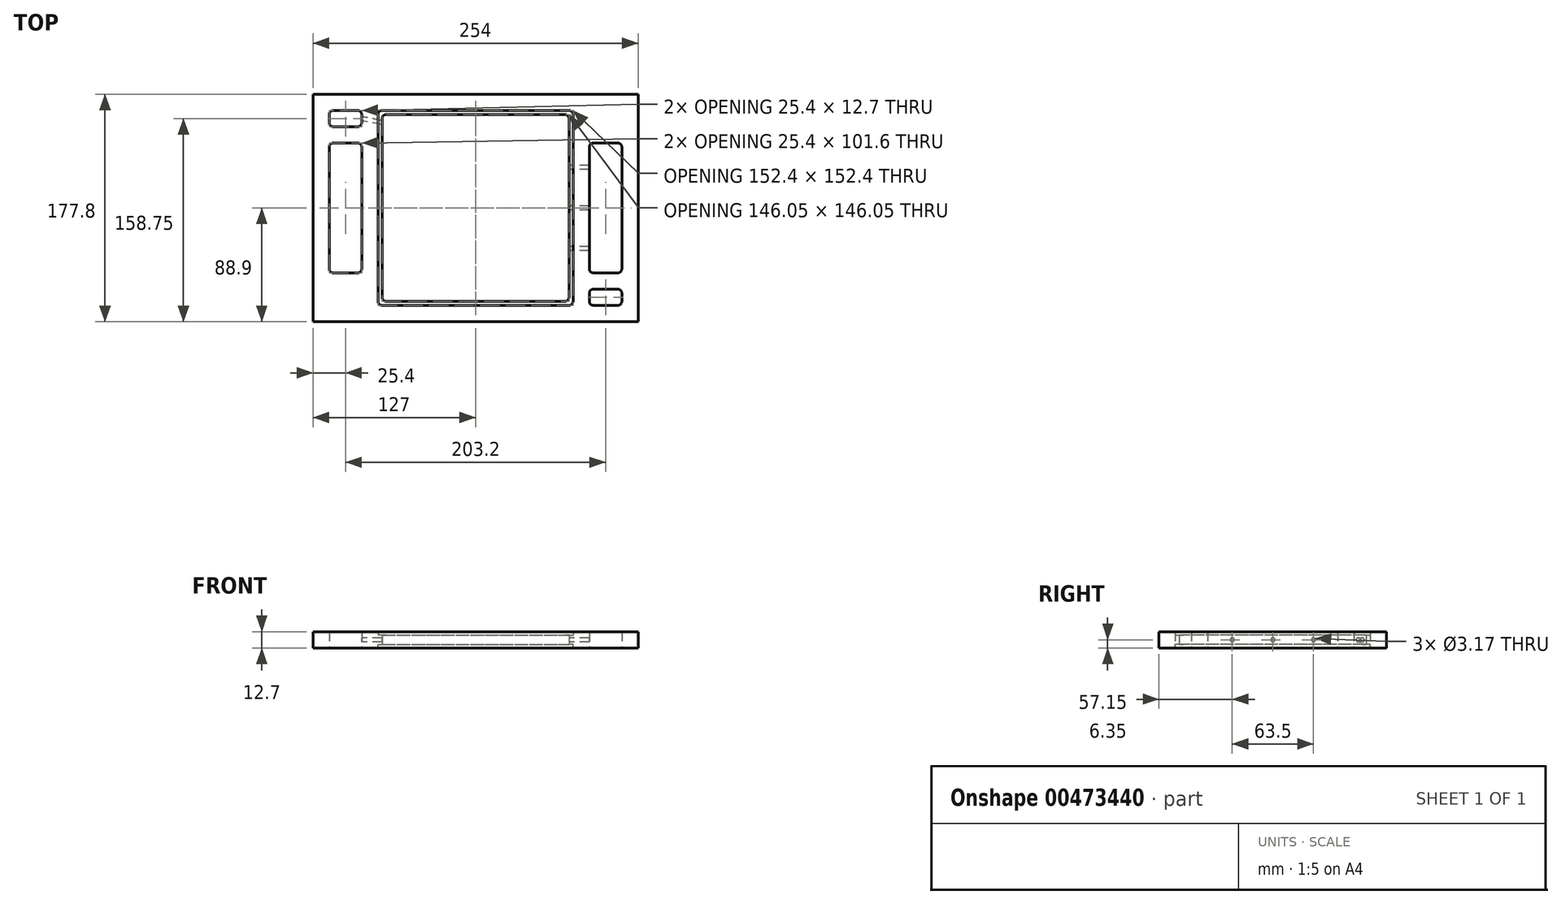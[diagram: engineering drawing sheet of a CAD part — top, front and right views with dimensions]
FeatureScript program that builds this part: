
annotation { "Feature Type Name" : "Feature", "Feature Type Description" : "" }
export const myFeature = defineFeature(function(context is Context, id is Id, definition is map)
    precondition{}
    {
        {
            var Q0;
            Q0=qCreatedBy(makeId("Top.planeOp"),FACE);
            var sketch = newSketch(context, id + "F0", { "sketchPlane" : qUnion([Q0])});
            skPoint(sketch, "E0.middle", {"position": v(0, 0) * mm});
            skLineSegment(sketch, "E1.bottom", {"start": v(-76.2, 76.2) * mm, "end": v(76.2, 76.2) * mm});
            skLineSegment(sketch, "E1.top", {"start": v(-76.2, -76.2) * mm, "end": v(76.2, -76.2) * mm});
            skLineSegment(sketch, "E1.left", {"start": v(-76.2, 76.2) * mm, "end": v(-76.2, -76.2) * mm});
            skLineSegment(sketch, "E1.right", {"start": v(76.2, 76.2) * mm, "end": v(76.2, -76.2) * mm});
            skLineSegment(sketch, "E2.bottom", {"start": v(-127, 88.9) * mm, "end": v(127, 88.9) * mm});
            skLineSegment(sketch, "E2.top", {"start": v(-127, -88.9) * mm, "end": v(127, -88.9) * mm});
            skLineSegment(sketch, "E2.left", {"start": v(-127, 88.9) * mm, "end": v(-127, -88.9) * mm});
            skLineSegment(sketch, "E2.right", {"start": v(127, 88.9) * mm, "end": v(127, -88.9) * mm});
            skLineSegment(sketch, "E3.bottom", {"start": v(-88.9, 76.2) * mm, "end": v(-114.3, 76.2) * mm});
            skLineSegment(sketch, "E3.top", {"start": v(-88.9, 63.5) * mm, "end": v(-114.3, 63.5) * mm});
            skLineSegment(sketch, "E3.left", {"start": v(-88.9, 76.2) * mm, "end": v(-88.9, 63.5) * mm});
            skLineSegment(sketch, "E3.right", {"start": v(-114.3, 76.2) * mm, "end": v(-114.3, 63.5) * mm});
            skLineSegment(sketch, "E4", {"start": v(0, 76.2) * mm, "end": v(0, -76.2) * mm, "construction": true});
            skLineSegment(sketch, "E5", {"start": v(-76.2, 0) * mm, "end": v(76.2, 0) * mm, "construction": true});
            skLineSegment(sketch, "E6.bottom", {"start": v(88.9, -76.2) * mm, "end": v(114.3, -76.2) * mm});
            skLineSegment(sketch, "E6.top", {"start": v(88.9, -63.5) * mm, "end": v(114.3, -63.5) * mm});
            skLineSegment(sketch, "E6.left", {"start": v(88.9, -76.2) * mm, "end": v(88.9, -63.5) * mm});
            skLineSegment(sketch, "E6.right", {"start": v(114.3, -76.2) * mm, "end": v(114.3, -63.5) * mm});
            skLineSegment(sketch, "E7.bottom", {"start": v(-88.9, 50.8) * mm, "end": v(-114.3, 50.8) * mm});
            skLineSegment(sketch, "E7.top", {"start": v(-88.9, -50.8) * mm, "end": v(-114.3, -50.8) * mm});
            skLineSegment(sketch, "E7.left", {"start": v(-88.9, 50.8) * mm, "end": v(-88.9, -50.8) * mm});
            skLineSegment(sketch, "E7.right", {"start": v(-114.3, 50.8) * mm, "end": v(-114.3, -50.8) * mm});
            skPoint(sketch, "E7.middle", {"position": v(-101.6, 0) * mm});
            skLineSegment(sketch, "E8.MirrorCS", {"start": v(88.9, 50.8) * mm, "end": v(114.3, 50.8) * mm});
            skLineSegment(sketch, "E9.MirrorCS", {"start": v(114.3, 50.8) * mm, "end": v(114.3, -50.8) * mm});
            skLineSegment(sketch, "E10.MirrorCS", {"start": v(88.9, 50.8) * mm, "end": v(88.9, -50.8) * mm});
            skLineSegment(sketch, "E11.MirrorCS", {"start": v(88.9, -50.8) * mm, "end": v(114.3, -50.8) * mm});
            skSolve(sketch);
        }
        {
            var Q0;
            Q0=makeQuery(id+"F0.imprint","IMPRINT",FACE,{"disambiguationData":[TD([[makeQuery(id+"F0.imprint","IMPRINT",EDGE,{"derivedFrom":sQuery(id+"F0.wireOp",EDGE,"E1.bottom")}),1.0]])]});
            extrude(context, id + "F1", {"entities" : qUnion([Q0]), "depth" : 6.35 * mm, "offsetDistance" : 25.4 * mm});
        }
        {
            var Q0;
            Q0=makeQuery(id+"F0.imprint","IMPRINT",FACE,{"disambiguationData":[TD([[makeQuery(id+"F0.imprint","IMPRINT",EDGE,{"derivedFrom":sQuery(id+"F0.wireOp",EDGE,"E1.bottom")}),-1.0]])]});
            var sketch = newSketch(context, id + "F2", { "sketchPlane" : qUnion([Q0])});
            skLineSegment(sketch, "E12.0", {"start": v(-76.2, 76.2) * mm, "end": v(76.2, 76.2) * mm});
            skLineSegment(sketch, "E12.1", {"start": v(-76.2, 76.2) * mm, "end": v(-76.2, -76.2) * mm});
            skLineSegment(sketch, "E12.2", {"start": v(76.2, 76.2) * mm, "end": v(76.2, -76.2) * mm});
            skLineSegment(sketch, "E12.3", {"start": v(-76.2, -76.2) * mm, "end": v(76.2, -76.2) * mm});
            skLineSegment(sketch, "E13.0", {"start": v(-73.03, 73.02) * mm, "end": v(73.03, 73.03) * mm});
            skLineSegment(sketch, "E13.1", {"start": v(-73.03, 73.02) * mm, "end": v(-73.03, -73.03) * mm});
            skLineSegment(sketch, "E13.2", {"start": v(-73.03, -73.03) * mm, "end": v(73.03, -73.02) * mm});
            skLineSegment(sketch, "E13.3", {"start": v(73.03, 73.03) * mm, "end": v(73.03, -73.02) * mm});
            skSolve(sketch);
        }
        {
            var Q0;
            Q0=makeQuery(id+"F2.imprint","IMPRINT",FACE,{"disambiguationData":[TD([[makeQuery(id+"F2.imprint","IMPRINT",EDGE,{"derivedFrom":sQuery(id+"F2.wireOp",EDGE,"E12.0")}),-1.0]])]});
            extrude(context, id + "F3", {"entities" : qUnion([Q0]), "operationType" : NewBodyOperationType.ADD, "depth" : 3.56 * mm, "offsetDistance" : 25.4 * mm});
        }
        {
            var Q0;
            {var subQ0=makeQuery(id+"F3.opExtrude","SWEPT_EDGE",EDGE,{"disambiguationData":[OSD([sQuery(id+"F2.wireOp",EDGE,"E13.0"),sQuery(id+"F2.wireOp",EDGE,"E13.1")])]});Q0=makeQuery(id+"F6.boolean.opBoolean","MERGE",EDGE,{"derivedFrom":[subQ0,makeQuery(id+"F6.opPattern","COPY",EDGE,{"derivedFrom":subQ0,"instanceName":"1"})]});}
            var Q1;
            Q1=makeQuery(id+"F1.opExtrude","SWEPT_EDGE",EDGE,{"disambiguationData":[OSD([sQuery(id+"F0.wireOp",EDGE,"E1.bottom"),sQuery(id+"F0.wireOp",EDGE,"E1.left")])]});
            var Q2;
            Q2=makeQuery(id+"F3.opExtrude","SWEPT_EDGE",EDGE,{"disambiguationData":[OSD([sQuery(id+"F2.wireOp",EDGE,"E13.0"),sQuery(id+"F2.wireOp",EDGE,"E13.3")])]});
            var Q3;
            Q3=makeQuery(id+"F1.opExtrude","SWEPT_EDGE",EDGE,{"disambiguationData":[OSD([sQuery(id+"F0.wireOp",EDGE,"E1.bottom"),sQuery(id+"F0.wireOp",EDGE,"E1.right")])]});
            var Q4;
            Q4=makeQuery(id+"F3.opExtrude","SWEPT_EDGE",EDGE,{"disambiguationData":[OSD([sQuery(id+"F2.wireOp",EDGE,"E13.1"),sQuery(id+"F2.wireOp",EDGE,"E13.2")])]});
            var Q5;
            Q5=makeQuery(id+"F1.opExtrude","SWEPT_EDGE",EDGE,{"disambiguationData":[OSD([sQuery(id+"F0.wireOp",EDGE,"E1.top"),sQuery(id+"F0.wireOp",EDGE,"E1.left")])]});
            var Q6;
            Q6=makeQuery(id+"F3.opExtrude","SWEPT_EDGE",EDGE,{"disambiguationData":[OSD([sQuery(id+"F2.wireOp",EDGE,"E13.2"),sQuery(id+"F2.wireOp",EDGE,"E13.3")])]});
            var Q7;
            Q7=makeQuery(id+"F1.opExtrude","SWEPT_EDGE",EDGE,{"disambiguationData":[OSD([sQuery(id+"F0.wireOp",EDGE,"E1.top"),sQuery(id+"F0.wireOp",EDGE,"E1.right")])]});
            fillet(context, id + "F4", {"entities" : qUnion([Q0, Q1, Q2, Q3, Q4, Q5, Q6, Q7]), "radius" : 3.17 * mm, "tangentPropagation" : true, "allowEdgeOverflow" : false});
        }
        {
            var Q0;
            Q0=makeQuery(id+"F1.opExtrude","SWEPT_EDGE",EDGE,{"disambiguationData":[OSD([sQuery(id+"F0.wireOp",EDGE,"E3.bottom"),sQuery(id+"F0.wireOp",EDGE,"E3.left")])]});
            var Q1;
            Q1=makeQuery(id+"F1.opExtrude","SWEPT_EDGE",EDGE,{"disambiguationData":[OSD([sQuery(id+"F0.wireOp",EDGE,"E3.top"),sQuery(id+"F0.wireOp",EDGE,"E3.left")])]});
            var Q2;
            Q2=makeQuery(id+"F1.opExtrude","SWEPT_EDGE",EDGE,{"disambiguationData":[OSD([sQuery(id+"F0.wireOp",EDGE,"E3.top"),sQuery(id+"F0.wireOp",EDGE,"E3.right")])]});
            var Q3;
            Q3=makeQuery(id+"F1.opExtrude","SWEPT_EDGE",EDGE,{"disambiguationData":[OSD([sQuery(id+"F0.wireOp",EDGE,"E3.bottom"),sQuery(id+"F0.wireOp",EDGE,"E3.right")])]});
            var Q4;
            Q4=makeQuery(id+"F1.opExtrude","SWEPT_EDGE",EDGE,{"disambiguationData":[OSD([sQuery(id+"F0.wireOp",EDGE,"E7.bottom"),sQuery(id+"F0.wireOp",EDGE,"E7.right")])]});
            var Q5;
            Q5=makeQuery(id+"F1.opExtrude","SWEPT_EDGE",EDGE,{"disambiguationData":[OSD([sQuery(id+"F0.wireOp",EDGE,"E7.bottom"),sQuery(id+"F0.wireOp",EDGE,"E7.left")])]});
            var Q6;
            Q6=makeQuery(id+"F1.opExtrude","SWEPT_EDGE",EDGE,{"disambiguationData":[OSD([sQuery(id+"F0.wireOp",EDGE,"E7.top"),sQuery(id+"F0.wireOp",EDGE,"E7.left")])]});
            var Q7;
            Q7=makeQuery(id+"F1.opExtrude","SWEPT_EDGE",EDGE,{"disambiguationData":[OSD([sQuery(id+"F0.wireOp",EDGE,"E7.top"),sQuery(id+"F0.wireOp",EDGE,"E7.right")])]});
            var Q8;
            Q8=makeQuery(id+"F1.opExtrude","SWEPT_EDGE",EDGE,{"disambiguationData":[OSD([sQuery(id+"F0.wireOp",EDGE,"E6.bottom"),sQuery(id+"F0.wireOp",EDGE,"E6.right")])]});
            var Q9;
            Q9=makeQuery(id+"F1.opExtrude","SWEPT_EDGE",EDGE,{"disambiguationData":[OSD([sQuery(id+"F0.wireOp",EDGE,"E6.bottom"),sQuery(id+"F0.wireOp",EDGE,"E6.left")])]});
            var Q10;
            Q10=makeQuery(id+"F1.opExtrude","SWEPT_EDGE",EDGE,{"disambiguationData":[OSD([sQuery(id+"F0.wireOp",EDGE,"E6.top"),sQuery(id+"F0.wireOp",EDGE,"E6.left")])]});
            var Q11;
            Q11=makeQuery(id+"F1.opExtrude","SWEPT_EDGE",EDGE,{"disambiguationData":[OSD([sQuery(id+"F0.wireOp",EDGE,"E6.top"),sQuery(id+"F0.wireOp",EDGE,"E6.right")])]});
            var Q12;
            Q12=makeQuery(id+"F1.opExtrude","SWEPT_EDGE",EDGE,{"disambiguationData":[OSD([sQuery(id+"F0.wireOp",EDGE,"E9.MirrorCS"),sQuery(id+"F0.wireOp",EDGE,"E11.MirrorCS")])]});
            var Q13;
            Q13=makeQuery(id+"F1.opExtrude","SWEPT_EDGE",EDGE,{"disambiguationData":[OSD([sQuery(id+"F0.wireOp",EDGE,"E10.MirrorCS"),sQuery(id+"F0.wireOp",EDGE,"E11.MirrorCS")])]});
            var Q14;
            Q14=makeQuery(id+"F1.opExtrude","SWEPT_EDGE",EDGE,{"disambiguationData":[OSD([sQuery(id+"F0.wireOp",EDGE,"E8.MirrorCS"),sQuery(id+"F0.wireOp",EDGE,"E10.MirrorCS")])]});
            var Q15;
            Q15=makeQuery(id+"F1.opExtrude","SWEPT_EDGE",EDGE,{"disambiguationData":[OSD([sQuery(id+"F0.wireOp",EDGE,"E8.MirrorCS"),sQuery(id+"F0.wireOp",EDGE,"E9.MirrorCS")])]});
            fillet(context, id + "F5", {"entities" : qUnion([Q0, Q1, Q2, Q3, Q4, Q5, Q6, Q7, Q8, Q9, Q10, Q11, Q12, Q13, Q14, Q15]), "radius" : 3.17 * mm, "allowEdgeOverflow" : false});
        }
        {
            var Q0;
            Q0=makeQuery(id+"F1.opExtrude","SWEPT_BODY",BODY,{"disambiguationData":[OSD([sQuery(id+"F0.wireOp",EDGE,"E1.bottom"),sQuery(id+"F0.wireOp",EDGE,"E1.top"),sQuery(id+"F0.wireOp",EDGE,"E1.left"),sQuery(id+"F0.wireOp",EDGE,"E1.right"),sQuery(id+"F0.wireOp",EDGE,"E2.bottom"),sQuery(id+"F0.wireOp",EDGE,"E2.top"),sQuery(id+"F0.wireOp",EDGE,"E2.left"),sQuery(id+"F0.wireOp",EDGE,"E2.right"),sQuery(id+"F0.wireOp",EDGE,"E3.bottom"),sQuery(id+"F0.wireOp",EDGE,"E3.top"),sQuery(id+"F0.wireOp",EDGE,"E3.left"),sQuery(id+"F0.wireOp",EDGE,"E3.right"),sQuery(id+"F0.wireOp",EDGE,"E6.bottom"),sQuery(id+"F0.wireOp",EDGE,"E6.top"),sQuery(id+"F0.wireOp",EDGE,"E6.left"),sQuery(id+"F0.wireOp",EDGE,"E6.right"),sQuery(id+"F0.wireOp",EDGE,"E7.bottom"),sQuery(id+"F0.wireOp",EDGE,"E7.top"),sQuery(id+"F0.wireOp",EDGE,"E7.left"),sQuery(id+"F0.wireOp",EDGE,"E7.right"),sQuery(id+"F0.wireOp",EDGE,"E8.MirrorCS"),sQuery(id+"F0.wireOp",EDGE,"E9.MirrorCS"),sQuery(id+"F0.wireOp",EDGE,"E10.MirrorCS"),sQuery(id+"F0.wireOp",EDGE,"E11.MirrorCS")])]});
            var Q1;
            Q1=makeQuery(id+"F0.imprint","IMPRINT",FACE,{"disambiguationData":[TD([[makeQuery(id+"F0.imprint","IMPRINT",EDGE,{"derivedFrom":sQuery(id+"F0.wireOp",EDGE,"E1.bottom")}),-1.0]])]});
            mirror(context, id + "F6", {"operationType" : NewBodyOperationType.ADD, "entities" : qUnion([Q0]), "mirrorPlane" : qUnion([Q1])});
        }
        {
            var Q0;
            {var subQ0=makeQuery(id+"F3.opExtrude","SWEPT_FACE",FACE,{"disambiguationData":[OSD([sQuery(id+"F2.wireOp",EDGE,"E13.3")])]});Q0=makeQuery(id+"F6.boolean.opBoolean","MERGE",FACE,{"derivedFrom":[subQ0,makeQuery(id+"F6.opPattern","COPY",FACE,{"derivedFrom":subQ0,"instanceName":"1"})]});}
            var sketch = newSketch(context, id + "F7", { "sketchPlane" : qUnion([Q0])});
            skLineSegment(sketch, "E14.0", {"start": v(-69.85, 0) * mm, "end": v(69.85, 0) * mm});
            skPoint(sketch, "E15", {"position": v(0, 0) * mm});
            skPoint(sketch, "E16", {"position": v(-31.75, 0) * mm});
            skPoint(sketch, "E17.MirrorP", {"position": v(31.75, 0) * mm});
            skSolve(sketch);
        }
        {
            var Q0;
            Q0=sQuery(id+"F7.wireOp",VERTEX,"E16");
            var Q1;
            Q1=sQuery(id+"F7.wireOp",VERTEX,"E15");
            var Q2;
            Q2=sQuery(id+"F7.wireOp",VERTEX,"E17.MirrorP");
            var Q3;
            Q3=makeQuery(id+"F1.opExtrude","SWEPT_BODY",BODY,{"disambiguationData":[OSD([sQuery(id+"F0.wireOp",EDGE,"E1.bottom"),sQuery(id+"F0.wireOp",EDGE,"E1.top"),sQuery(id+"F0.wireOp",EDGE,"E1.left"),sQuery(id+"F0.wireOp",EDGE,"E1.right"),sQuery(id+"F0.wireOp",EDGE,"E2.bottom"),sQuery(id+"F0.wireOp",EDGE,"E2.top"),sQuery(id+"F0.wireOp",EDGE,"E2.left"),sQuery(id+"F0.wireOp",EDGE,"E2.right"),sQuery(id+"F0.wireOp",EDGE,"E3.bottom"),sQuery(id+"F0.wireOp",EDGE,"E3.top"),sQuery(id+"F0.wireOp",EDGE,"E3.left"),sQuery(id+"F0.wireOp",EDGE,"E3.right"),sQuery(id+"F0.wireOp",EDGE,"E6.bottom"),sQuery(id+"F0.wireOp",EDGE,"E6.top"),sQuery(id+"F0.wireOp",EDGE,"E6.left"),sQuery(id+"F0.wireOp",EDGE,"E6.right"),sQuery(id+"F0.wireOp",EDGE,"E7.bottom"),sQuery(id+"F0.wireOp",EDGE,"E7.top"),sQuery(id+"F0.wireOp",EDGE,"E7.left"),sQuery(id+"F0.wireOp",EDGE,"E7.right"),sQuery(id+"F0.wireOp",EDGE,"E8.MirrorCS"),sQuery(id+"F0.wireOp",EDGE,"E9.MirrorCS"),sQuery(id+"F0.wireOp",EDGE,"E10.MirrorCS"),sQuery(id+"F0.wireOp",EDGE,"E11.MirrorCS")])]});
            hole(context, id + "F8", {"style" : HoleStyle.SIMPLE, "endStyle" : HoleEndStyle.BLIND, "holeDiameter" : 3.17 * mm, "majorDiameter" : 6.35 * mm, "holeDepth" : 19.05 * mm, "isTappedThrough" : true, "tappedDepth" : 12.7 * mm, "tapClearance" : 3, "startFromSketch" : true, "locations" : qUnion([Q0, Q1, Q2]), "scope" : qUnion([Q3])});
        }
        {
            var Q0;
            {var subQ0=makeQuery(id+"F3.opExtrude","SWEPT_FACE",FACE,{"disambiguationData":[OSD([sQuery(id+"F2.wireOp",EDGE,"E13.1")])]});Q0=makeQuery(id+"F6.boolean.opBoolean","MERGE",FACE,{"derivedFrom":[subQ0,makeQuery(id+"F6.opPattern","COPY",FACE,{"derivedFrom":subQ0,"instanceName":"1"})]});}
            var sketch = newSketch(context, id + "F9", { "sketchPlane" : qUnion([Q0])});
            skPoint(sketch, "E18", {"position": v(66.67, 0) * mm});
            skPoint(sketch, "E18.positionSnap0", {"position": v(69.85, 0) * mm});
            skSolve(sketch);
        }
        {
            var Q0;
            Q0=makeQuery(id+"F0.imprint","IMPRINT",FACE,{"disambiguationData":[TD([[makeQuery(id+"F0.imprint","IMPRINT",EDGE,{"derivedFrom":sQuery(id+"F0.wireOp",EDGE,"E3.bottom")}),1.0]])]});
            var sketch = newSketch(context, id + "F10", { "sketchPlane" : qUnion([Q0])});
            skPoint(sketch, "E19.0", {"position": v(-88.9, 69.85) * mm});
            skPoint(sketch, "E20.0", {"position": v(-73.03, 66.67) * mm});
            skLineSegment(sketch, "E21", {"start": v(-69.91, 66.05) * mm, "end": v(-92.01, 70.47) * mm});
            skSolve(sketch);
        }
        {
            var Q0;
            Q0=sQuery(id+"F10.wireOp",EDGE,"E21");
            var Q1;
            Q1=sQuery(id+"F9.wireOp",VERTEX,"E18");
            cPlane(context, id + "F11", {"entities" : qUnion([Q0, Q1]), "cplaneType" : CPlaneType.LINE_POINT, "offset" : 25.4 * mm, "width" : 152.4 * mm, "height" : 152.4 * mm});
        }
        {
            var Q0;
            Q0=qCreatedBy(id+"F11.planeOp",FACE);
            var sketch = newSketch(context, id + "F12", { "sketchPlane" : qUnion([Q0])});
            skPoint(sketch, "E22.0", {"position": v(-51.06, 0) * mm});
            skCircle(sketch, "E23", {"center": v(-51.06, 0) * mm, "radius": 1.59 * mm});
            skSolve(sketch);
        }
        {
            var Q0;
            Q0=makeQuery(id+"F12.imprint","IMPRINT",FACE,{"disambiguationData":[TD([[makeQuery(id+"F12.imprint","IMPRINT",EDGE,{"derivedFrom":sQuery(id+"F12.wireOp",EDGE,"E23")}),1.0]])]});
            var Q1;
            Q1=sQuery(id+"F10.wireOp",EDGE,"E21");
            sweep(context, id + "F13", {"operationType" : NewBodyOperationType.REMOVE, "profiles" : qUnion([Q0]), "path" : qUnion([Q1])});
        }
    });
